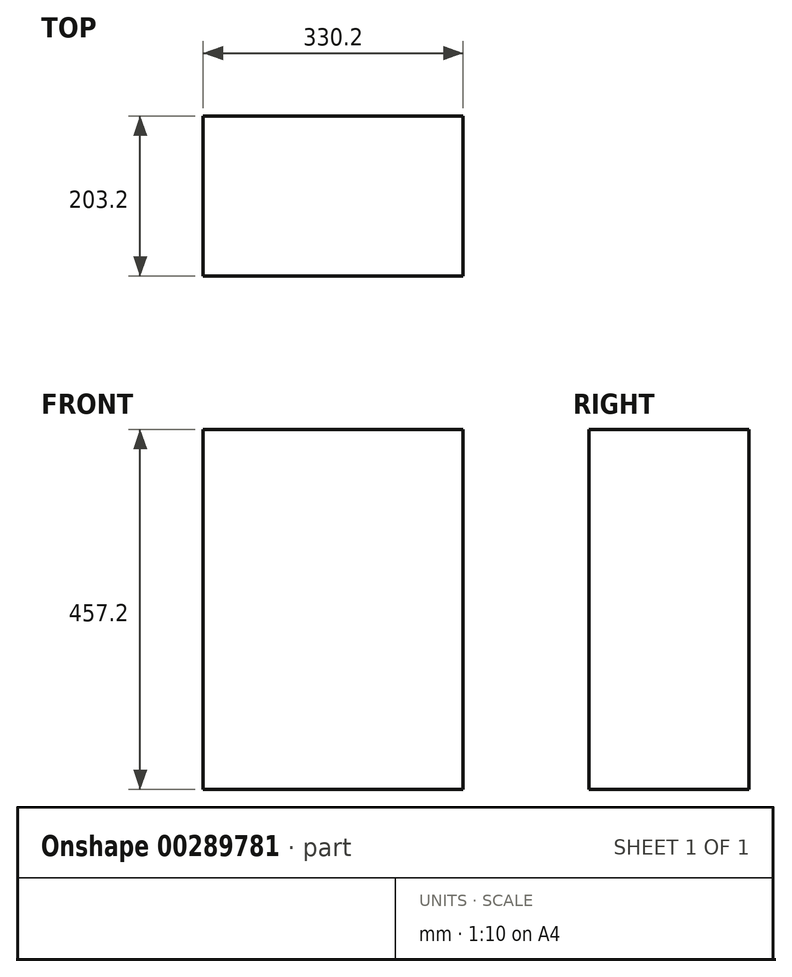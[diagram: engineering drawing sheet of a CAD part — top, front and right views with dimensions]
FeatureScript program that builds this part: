
annotation { "Feature Type Name" : "Feature", "Feature Type Description" : "" }
export const myFeature = defineFeature(function(context is Context, id is Id, definition is map)
    precondition{}
    {
        {
            var Q0;
            Q0=qCreatedBy(makeId("Top.planeOp"),FACE);
            var sketch = newSketch(context, id + "F0", { "sketchPlane" : qUnion([Q0])});
            skLineSegment(sketch, "E0.bottom", {"start": v(0, 0) * mm, "end": v(330.2, 0) * mm});
            skLineSegment(sketch, "E0.top", {"start": v(0, 203.2) * mm, "end": v(330.2, 203.2) * mm});
            skLineSegment(sketch, "E0.left", {"start": v(0, 0) * mm, "end": v(0, 203.2) * mm});
            skLineSegment(sketch, "E0.right", {"start": v(330.2, 0) * mm, "end": v(330.2, 203.2) * mm});
            skSolve(sketch);
        }
        {
            var Q0;
            Q0=makeQuery(id+"F0.imprint","IMPRINT",FACE,{"disambiguationData":[TD([[makeQuery(id+"F0.imprint","IMPRINT",EDGE,{"derivedFrom":sQuery(id+"F0.wireOp",EDGE,"E0.bottom")}),1.0]])]});
            extrude(context, id + "F1", {"entities" : qUnion([Q0]), "depth" : 457.2 * mm});
        }
    });
